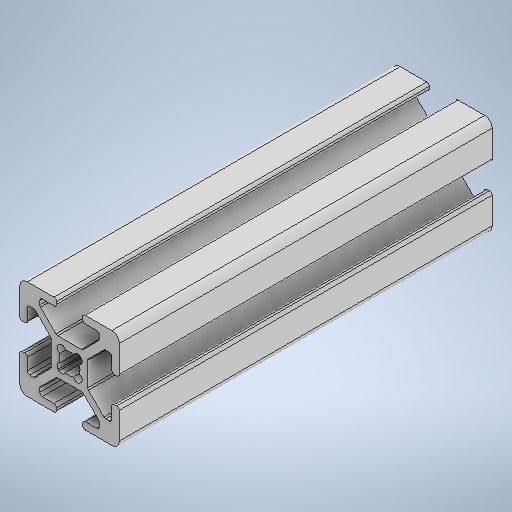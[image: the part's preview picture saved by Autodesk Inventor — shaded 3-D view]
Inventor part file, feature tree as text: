
AUTODESK INVENTOR PART (.ipt)
format: ipt  version: 2025 (Build 290162000, 162)  size: 367,104 bytes
history: native  units: mm
features: extrude x1, sketch x1
ambient origin geometry x8: Origin, YZ Plane, XZ Plane, XY Plane, X Axis, Y Axis, Z Axis, Center Point
bodies: Solid1 (feature_tree)
feature tree (2):
  extrude  "Extrusion1"  Depth=75.0mm
  sketch  "Sketch1"  dims[d0=75.0mm d1=0.0mm d2=1.0mm d3=1.0mm d4=1.0mm d5=0.15mm d6=0.25mm d7=0.375mm d8=14.3117mm d9=0.75mm d10=20.594885mm d11=0.0625mm d12=0.75mm d13=0.375mm]
